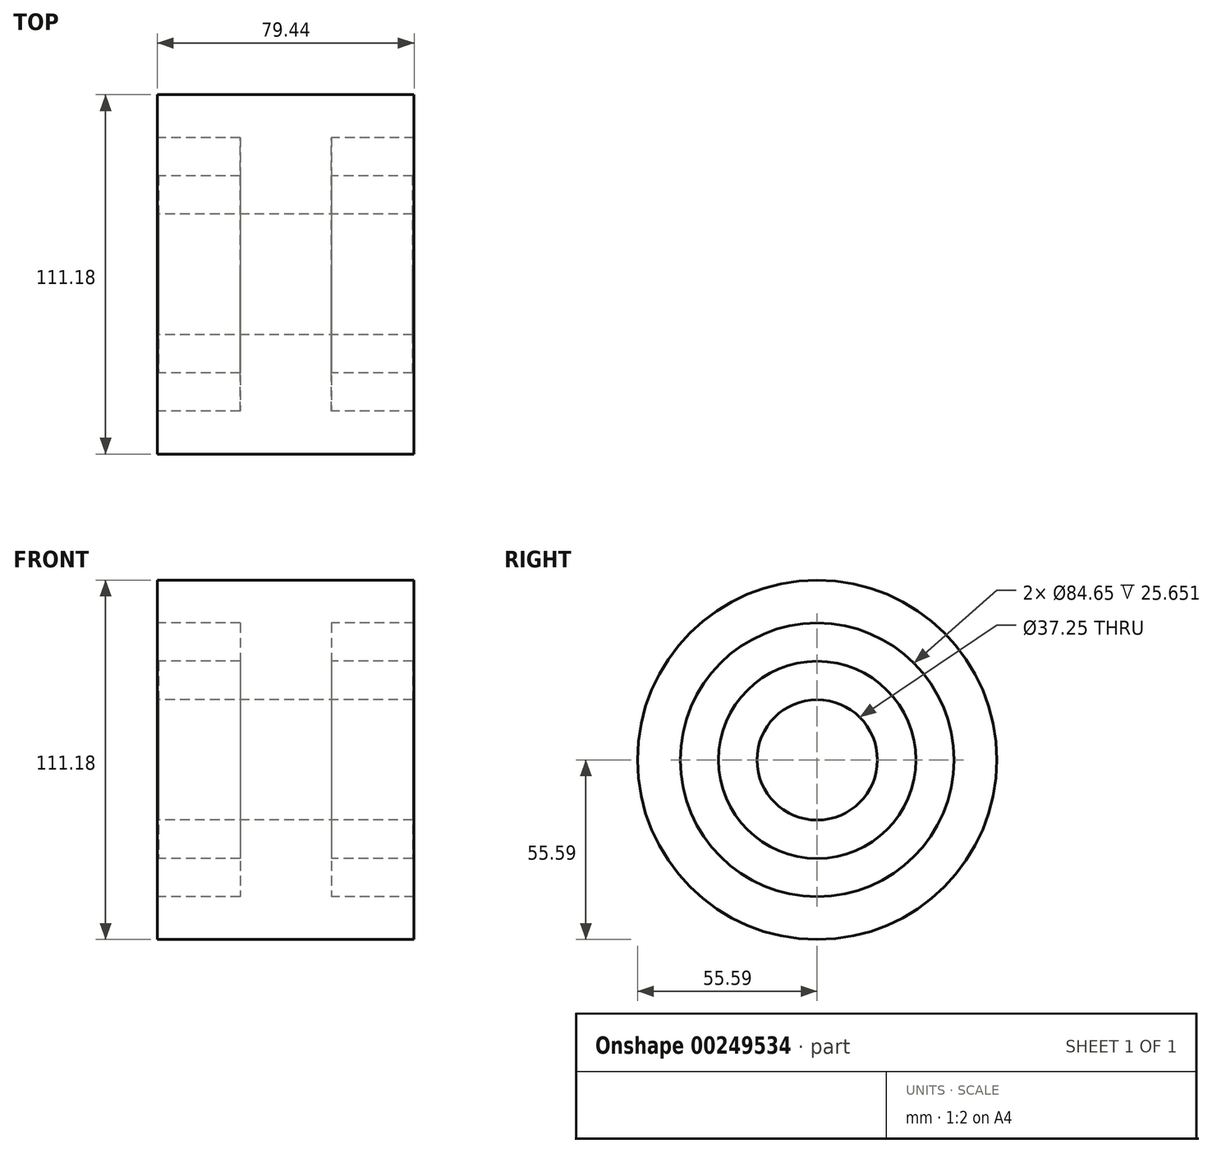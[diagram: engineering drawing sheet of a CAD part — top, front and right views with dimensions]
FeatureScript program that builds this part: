
annotation { "Feature Type Name" : "Feature", "Feature Type Description" : "" }
export const myFeature = defineFeature(function(context is Context, id is Id, definition is map)
    precondition{}
    {
        {
            var Q0;
            Q0=qCreatedBy(makeId("Front.planeOp"),FACE);
            var sketch = newSketch(context, id + "F1", { "sketchPlane" : qUnion([Q0])});
            skLineSegment(sketch, "E0", {"start": v(-78.06, 0) * mm, "end": v(83.52, 0) * mm, "construction": true});
            skLineSegment(sketch, "E1", {"start": v(0, 80.44) * mm, "end": v(0, -92.76) * mm, "construction": true});
            skLineSegment(sketch, "E2", {"start": v(0, 55.59) * mm, "end": v(39.72, 55.59) * mm});
            skLineSegment(sketch, "E3", {"start": v(39.72, 55.59) * mm, "end": v(39.72, 42.32) * mm});
            skLineSegment(sketch, "E4", {"start": v(39.72, 42.32) * mm, "end": v(14.07, 42.32) * mm});
            skLineSegment(sketch, "E5", {"start": v(14.07, 30.52) * mm, "end": v(14.07, 42.32) * mm});
            skLineSegment(sketch, "E6", {"start": v(14.07, 30.52) * mm, "end": v(39.33, 30.52) * mm});
            skLineSegment(sketch, "E7", {"start": v(39.33, 30.52) * mm, "end": v(39.33, 18.62) * mm});
            skLineSegment(sketch, "E8", {"start": v(0, 18.62) * mm, "end": v(0, 18.62) * mm});
            skLineSegment(sketch, "E9", {"start": v(39.33, 18.62) * mm, "end": v(0, 18.62) * mm});
            skLineSegment(sketch, "E10.MirrorCS", {"start": v(0, 55.59) * mm, "end": v(-39.72, 55.59) * mm});
            skLineSegment(sketch, "E11.MirrorCS", {"start": v(-39.72, 55.59) * mm, "end": v(-39.72, 42.32) * mm});
            skLineSegment(sketch, "E12.MirrorCS", {"start": v(-39.72, 42.32) * mm, "end": v(-14.07, 42.32) * mm});
            skLineSegment(sketch, "E13.MirrorCS", {"start": v(-14.07, 30.52) * mm, "end": v(-14.07, 42.32) * mm});
            skLineSegment(sketch, "E14.MirrorCS", {"start": v(-14.07, 30.52) * mm, "end": v(-39.33, 30.52) * mm});
            skLineSegment(sketch, "E15.MirrorCS", {"start": v(-39.33, 30.52) * mm, "end": v(-39.33, 18.62) * mm});
            skLineSegment(sketch, "E16.MirrorCS", {"start": v(-39.33, 18.62) * mm, "end": v(0, 18.62) * mm});
            skSolve(sketch);
        }
        {
            var Q0;
            Q0 = qSketchRegion(id + "F1", true);
            var Q1;
            Q1=sQuery(id+"F1.wireOp",EDGE,"E0");
            revolve(context, id + "F0", {"entities" : qUnion([Q0]), "axis" : qUnion([Q1]), "revolveType" : RevolveType.FULL});
        }
    });
